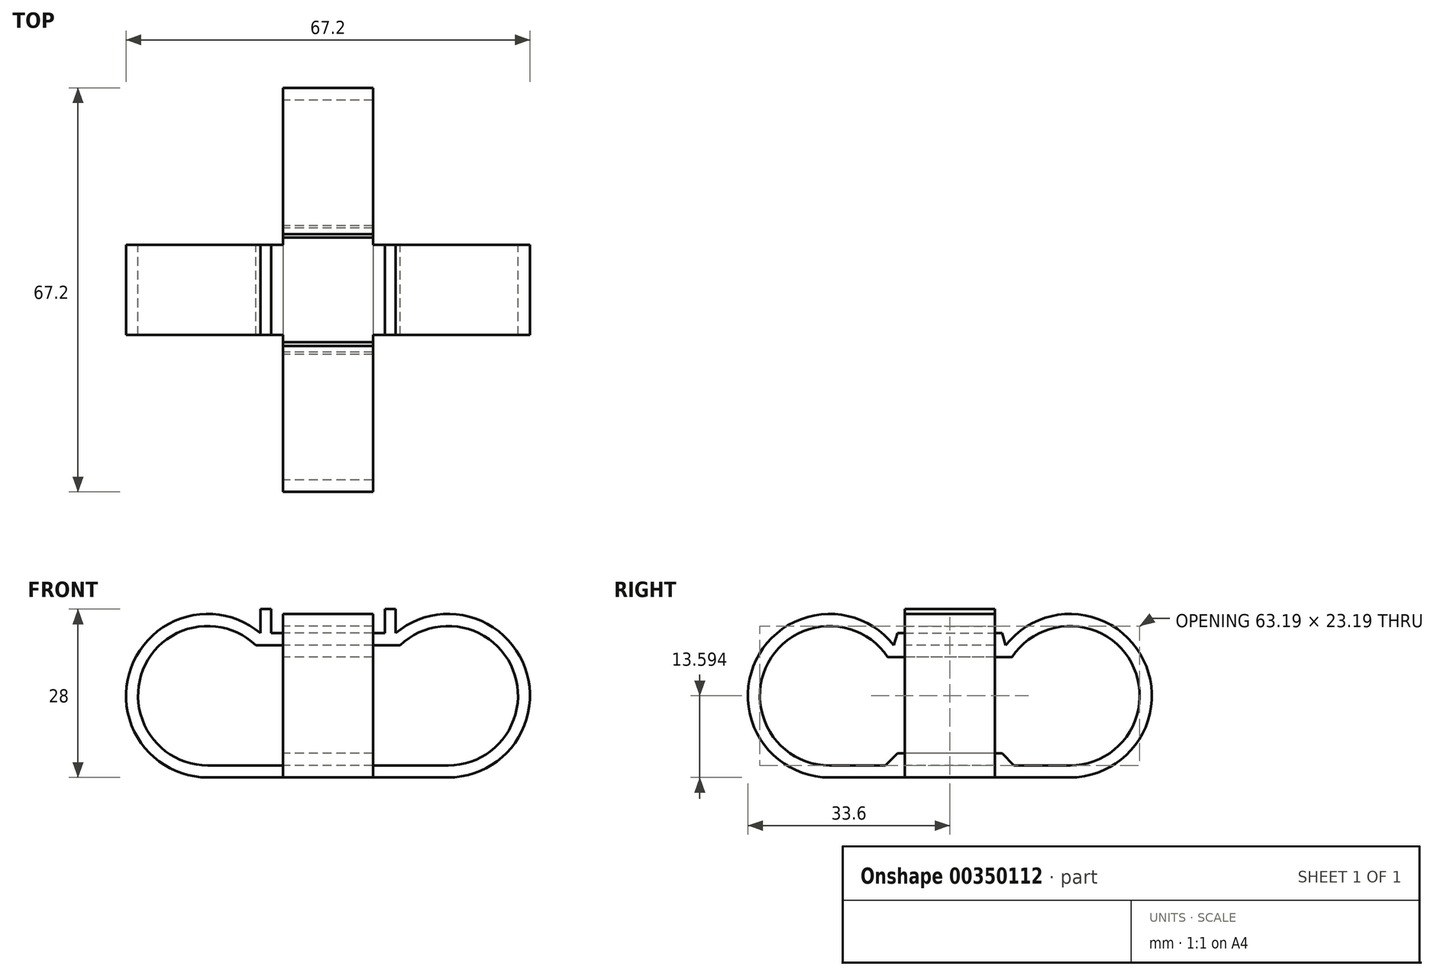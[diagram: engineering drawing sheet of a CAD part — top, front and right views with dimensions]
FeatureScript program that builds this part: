
annotation { "Feature Type Name" : "Feature", "Feature Type Description" : "" }
export const myFeature = defineFeature(function(context is Context, id is Id, definition is map)
    precondition{}
    {
        {
            var Q0;
            Q0=qCreatedBy(makeId("Front.planeOp"),FACE);
            var sketch = newSketch(context, id + "F0", { "sketchPlane" : qUnion([Q0])});
            skLineSegment(sketch, "E0.bottom", {"start": v(12, 10) * mm, "end": v(-12, 10) * mm});
            skLineSegment(sketch, "E0.top", {"start": v(20, -10) * mm, "end": v(-20, -10) * mm});
            skPoint(sketch, "E0.middle", {"position": v(0, 0) * mm});
            skArc(sketch, "E1", {"start": v(-20, -10) * mm, "mid": v(-30.77, 5.9) * mm, "end": v(-12, 10) * mm});
            skPoint(sketch, "E2.orphan", {"position": v(-20, 10) * mm});
            skArc(sketch, "E3.MirrorCS", {"start": v(20, -10) * mm, "mid": v(30.77, 5.9) * mm, "end": v(12, 10) * mm});
            skPoint(sketch, "E4.orphan", {"position": v(20, 10) * mm});
            skLineSegment(sketch, "E5.0", {"start": v(9.44, 12) * mm, "end": v(-9.44, 12) * mm});
            skArc(sketch, "E5.1", {"start": v(20, -12) * mm, "mid": v(32.77, 6.26) * mm, "end": v(11.24, 12) * mm});
            skLineSegment(sketch, "E5.2", {"start": v(20, -12) * mm, "end": v(-20, -12) * mm});
            skArc(sketch, "E5.3", {"start": v(-20, -12) * mm, "mid": v(-32.77, 6.26) * mm, "end": v(-11.24, 12) * mm});
            skLineSegment(sketch, "E6", {"start": v(-11.24, 12) * mm, "end": v(-11.24, 16) * mm});
            skLineSegment(sketch, "E7", {"start": v(-11.24, 16) * mm, "end": v(-9.44, 16) * mm});
            skLineSegment(sketch, "E8", {"start": v(-9.44, 16) * mm, "end": v(-9.44, 12) * mm});
            skLineSegment(sketch, "E9.MirrorCS", {"start": v(9.44, 16) * mm, "end": v(9.44, 12) * mm});
            skLineSegment(sketch, "E10.MirrorCS", {"start": v(11.24, 16) * mm, "end": v(9.44, 16) * mm});
            skLineSegment(sketch, "E11.MirrorCS", {"start": v(11.24, 12) * mm, "end": v(11.24, 16) * mm});
            skSolve(sketch);
        }
        {
            var Q0;
            Q0=qSketchRegion(id+"F0",true);
            extrude(context, id + "F1", {"entities" : qUnion([Q0]), "endBound" : BoundingType.SYMMETRIC, "depth" : 15 * mm});
        }
        {
            var Q0;
            Q0=qCreatedBy(makeId("Right.planeOp"),FACE);
            var sketch = newSketch(context, id + "F2", { "sketchPlane" : qUnion([Q0])});
            skLineSegment(sketch, "E12.top", {"start": v(7.5, -10) * mm, "end": v(-7.5, -10) * mm});
            skPoint(sketch, "E12.middle", {"position": v(0, 0) * mm});
            skArc(sketch, "E13", {"start": v(-20, -10) * mm, "mid": v(-30.22, 7.1) * mm, "end": v(-10.33, 8) * mm});
            skLineSegment(sketch, "E14.2", {"start": v(20, -12) * mm, "end": v(7.5, -12) * mm});
            skArc(sketch, "E14.3", {"start": v(-20, -12) * mm, "mid": v(-32.23, 7.55) * mm, "end": v(-9.3, 10) * mm});
            skLineSegment(sketch, "E15.0", {"start": v(10.33, 8) * mm, "end": v(-10.33, 8) * mm});
            skLineSegment(sketch, "E16.0", {"start": v(8.7, -8) * mm, "end": v(-8.7, -8) * mm});
            skPoint(sketch, "E17.orphan", {"position": v(-12, 10) * mm});
            skPoint(sketch, "E18.start.orphan", {"position": v(-20, 15.2) * mm});
            skLineSegment(sketch, "E19", {"start": v(-9.3, 10) * mm, "end": v(-8.7, 12) * mm});
            skLineSegment(sketch, "E20.0", {"start": v(-7.5, -12) * mm, "end": v(-7.5, 15.2) * mm, "construction": true});
            skLineSegment(sketch, "E20.1", {"start": v(7.5, -12) * mm, "end": v(7.5, 15.2) * mm, "construction": true});
            skLineSegment(sketch, "E21", {"start": v(-8.7, 12) * mm, "end": v(-7.5, 12) * mm});
            skLineSegment(sketch, "E22", {"start": v(-7.5, 12) * mm, "end": v(-7.5, 10) * mm});
            skLineSegment(sketch, "E23", {"start": v(-7.5, -12) * mm, "end": v(-20, -12) * mm});
            skLineSegment(sketch, "E24", {"start": v(7.5, -12) * mm, "end": v(-7.5, -12) * mm, "construction": true});
            skLineSegment(sketch, "E25", {"start": v(-8.7, -8) * mm, "end": v(-10.7, -10) * mm});
            skLineSegment(sketch, "E26", {"start": v(-10.7, -10) * mm, "end": v(-20, -10) * mm});
            skLineSegment(sketch, "E27.trimOffspring", {"start": v(-7.5, 12) * mm, "end": v(-8.7, 12) * mm});
            skLineSegment(sketch, "E28.MirrorCS", {"start": v(8.7, 12) * mm, "end": v(7.5, 12) * mm});
            skLineSegment(sketch, "E29.MirrorCS", {"start": v(7.5, 12) * mm, "end": v(8.7, 12) * mm});
            skLineSegment(sketch, "E30.MirrorCS", {"start": v(7.5, 12) * mm, "end": v(7.5, 10) * mm});
            skLineSegment(sketch, "E31.MirrorCS", {"start": v(8.7, -8) * mm, "end": v(10.7, -10) * mm});
            skLineSegment(sketch, "E32.MirrorCS", {"start": v(10.7, -10) * mm, "end": v(20, -10) * mm});
            skLineSegment(sketch, "E33.MirrorCS", {"start": v(9.3, 10) * mm, "end": v(8.7, 12) * mm});
            skPoint(sketch, "E34.MirrorP", {"position": v(20, 15.2) * mm});
            skArc(sketch, "E35.MirrorCS", {"start": v(20, -12) * mm, "mid": v(32.23, 7.55) * mm, "end": v(9.3, 10) * mm});
            skArc(sketch, "E36.MirrorCS", {"start": v(20, -10) * mm, "mid": v(30.22, 7.1) * mm, "end": v(10.33, 8) * mm});
            skLineSegment(sketch, "E37.MirrorCS", {"start": v(7.5, -12) * mm, "end": v(20, -12) * mm});
            skLineSegment(sketch, "E38.trimOffspring", {"start": v(7.5, 10) * mm, "end": v(-7.5, 10) * mm});
            skPoint(sketch, "E12.bottom.start.orphan", {"position": v(12, 10) * mm});
            skLineSegment(sketch, "E39", {"start": v(7.5, -12) * mm, "end": v(7.5, -10) * mm});
            skLineSegment(sketch, "E40", {"start": v(-7.5, -12) * mm, "end": v(-7.5, -10) * mm});
            skSolve(sketch);
        }
        {
            var Q0;
            Q0=qSketchRegion(id+"F2",true);
            extrude(context, id + "F3", {"entities" : qUnion([Q0]), "operationType" : NewBodyOperationType.ADD, "endBound" : BoundingType.SYMMETRIC, "depth" : 15 * mm});
        }
    });
